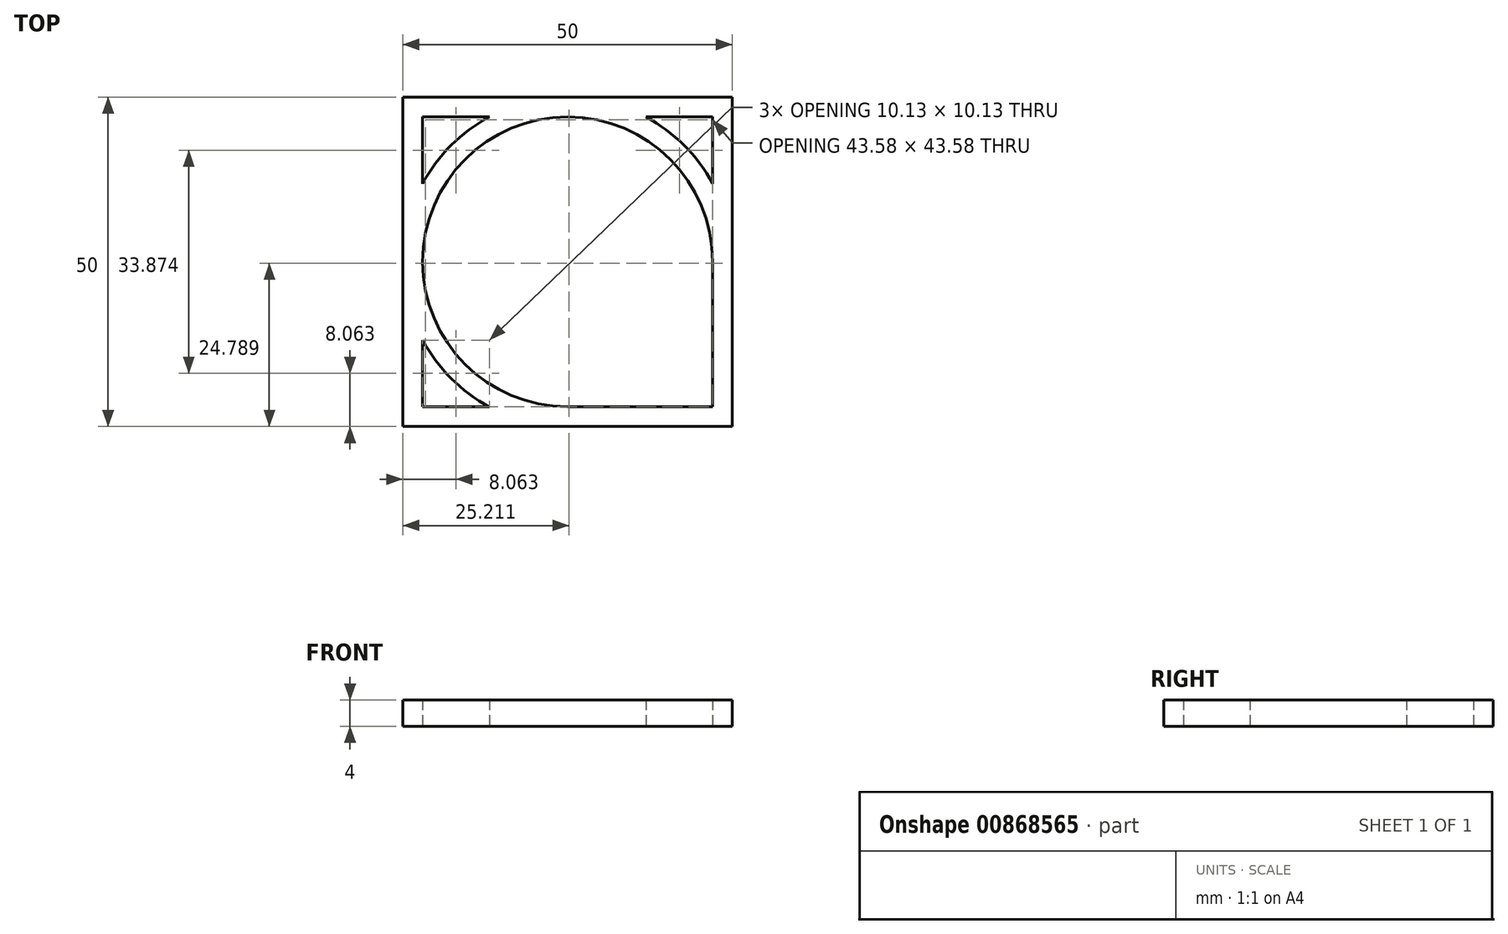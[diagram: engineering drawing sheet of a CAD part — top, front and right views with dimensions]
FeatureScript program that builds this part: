
annotation { "Feature Type Name" : "Feature", "Feature Type Description" : "" }
export const myFeature = defineFeature(function(context is Context, id is Id, definition is map)
    precondition{}
    {
        {
            var Q0;
            Q0=qCreatedBy(makeId("Top.planeOp"),FACE);
            var sketch = newSketch(context, id + "F0", { "sketchPlane" : qUnion([Q0])});
            skLineSegment(sketch, "E0.bottom", {"start": v(0, 0) * mm, "end": v(-50, 0) * mm});
            skLineSegment(sketch, "E0.top", {"start": v(0, 50) * mm, "end": v(-50, 50) * mm});
            skLineSegment(sketch, "E0.left", {"start": v(0, 0) * mm, "end": v(0, 50) * mm});
            skLineSegment(sketch, "E0.right", {"start": v(-50, 0) * mm, "end": v(-50, 50) * mm});
            skLineSegment(sketch, "E1", {"start": v(-25, 61.82) * mm, "end": v(-25, -11.65) * mm, "construction": true});
            skPoint(sketch, "E1.startSnap0", {"position": v(-25, 50) * mm});
            skLineSegment(sketch, "E2", {"start": v(-54.83, 25) * mm, "end": v(11.47, 25) * mm, "construction": true});
            skPoint(sketch, "E2.startSnap0", {"position": v(-50, 25) * mm});
            skCircle(sketch, "E3", {"center": v(-25, 25) * mm, "radius": 25 * mm});
            skCircle(sketch, "E4.0", {"center": v(-25, 25) * mm, "radius": 22 * mm});
            skLineSegment(sketch, "E5.0", {"start": v(-47, 3) * mm, "end": v(-47, 47) * mm});
            skLineSegment(sketch, "E5.1", {"start": v(-3, 3) * mm, "end": v(-47, 3) * mm});
            skLineSegment(sketch, "E5.2", {"start": v(-3, 3) * mm, "end": v(-3, 47) * mm});
            skLineSegment(sketch, "E5.3", {"start": v(-3, 47) * mm, "end": v(-47, 47) * mm});
            skSolve(sketch);
        }
        {
            var Q0;
            {var subQ1=sQuery(id+"F0.wireOp",EDGE,"E0.top");var subQ5=sQuery(id+"F0.wireOp",EDGE,"E0.right");var subQ6=makeQuery(id+"F0.imprint","INTERSECT",VERTEX,{"derivedFrom":[subQ1,subQ5]});Q0=makeQuery(id+"F0.imprint","IMPRINT",FACE,{"disambiguationData":[TD([[makeQuery(id+"F0.imprint","IMPRINT",EDGE,{"disambiguationData":[TD([[subQ6,1.0]])],"derivedFrom":subQ1}),1.0]])]});}
            var Q1;
            {var subQ0=sQuery(id+"F0.wireOp",EDGE,"E3");var subQ1=makeQuery(id+"F0.imprint","INTERSECT",VERTEX,{"derivedFrom":[sQuery(id+"F0.wireOp",EDGE,"E0.right"),subQ0]});Q1=makeQuery(id+"F0.imprint","IMPRINT",FACE,{"disambiguationData":[TD([[makeQuery(id+"F0.imprint","IMPRINT",EDGE,{"disambiguationData":[TD([[subQ1,1.0]])],"derivedFrom":subQ0}),1.0]])]});}
            var Q2;
            {var subQ1=sQuery(id+"F0.wireOp",EDGE,"E0.right");var subQ5=sQuery(id+"F0.wireOp",EDGE,"E0.bottom");var subQ9=makeQuery(id+"F0.imprint","INTERSECT",VERTEX,{"derivedFrom":[subQ5,subQ1]});Q2=makeQuery(id+"F0.imprint","IMPRINT",FACE,{"disambiguationData":[TD([[makeQuery(id+"F0.imprint","IMPRINT",EDGE,{"disambiguationData":[TD([[subQ9,1.0]])],"derivedFrom":subQ5}),-1.0]])]});}
            var Q3;
            {var subQ0=sQuery(id+"F0.wireOp",EDGE,"E3");var subQ1=makeQuery(id+"F0.imprint","INTERSECT",VERTEX,{"derivedFrom":[sQuery(id+"F0.wireOp",EDGE,"E0.bottom"),subQ0]});Q3=makeQuery(id+"F0.imprint","IMPRINT",FACE,{"disambiguationData":[TD([[makeQuery(id+"F0.imprint","IMPRINT",EDGE,{"disambiguationData":[TD([[subQ1,1.0]])],"derivedFrom":subQ0}),1.0]])]});}
            var Q4;
            {var subQ1=sQuery(id+"F0.wireOp",EDGE,"E0.bottom");var subQ7=sQuery(id+"F0.wireOp",EDGE,"E0.left");var subQ10=makeQuery(id+"F0.imprint","INTERSECT",VERTEX,{"derivedFrom":[subQ1,subQ7]});Q4=makeQuery(id+"F0.imprint","IMPRINT",FACE,{"disambiguationData":[TD([[makeQuery(id+"F0.imprint","IMPRINT",EDGE,{"disambiguationData":[TD([[subQ10,-1.0]])],"derivedFrom":subQ1}),-1.0]])]});}
            var Q5;
            {var subQ0=sQuery(id+"F0.wireOp",EDGE,"E3");var subQ1=makeQuery(id+"F0.imprint","INTERSECT",VERTEX,{"derivedFrom":[sQuery(id+"F0.wireOp",EDGE,"E0.left"),subQ0]});Q5=makeQuery(id+"F0.imprint","IMPRINT",FACE,{"disambiguationData":[TD([[makeQuery(id+"F0.imprint","IMPRINT",EDGE,{"disambiguationData":[TD([[subQ1,-1.0]])],"derivedFrom":subQ0}),1.0]])]});}
            var Q6;
            {var subQ1=sQuery(id+"F0.wireOp",EDGE,"E0.left");var subQ5=sQuery(id+"F0.wireOp",EDGE,"E0.top");var subQ9=makeQuery(id+"F0.imprint","INTERSECT",VERTEX,{"derivedFrom":[subQ5,subQ1]});Q6=makeQuery(id+"F0.imprint","IMPRINT",FACE,{"disambiguationData":[TD([[makeQuery(id+"F0.imprint","IMPRINT",EDGE,{"disambiguationData":[TD([[subQ9,-1.0]])],"derivedFrom":subQ5}),1.0]])]});}
            var Q7;
            {var subQ0=sQuery(id+"F0.wireOp",EDGE,"E3");var subQ1=makeQuery(id+"F0.imprint","INTERSECT",VERTEX,{"derivedFrom":[sQuery(id+"F0.wireOp",EDGE,"E0.top"),subQ0]});Q7=makeQuery(id+"F0.imprint","IMPRINT",FACE,{"disambiguationData":[TD([[makeQuery(id+"F0.imprint","IMPRINT",EDGE,{"disambiguationData":[TD([[subQ1,1.0]])],"derivedFrom":subQ0}),1.0]])]});}
            var Q8;
            {var subQ0=sQuery(id+"F0.wireOp",EDGE,"E5.3");var subQ1=sQuery(id+"F0.wireOp",EDGE,"E3");var subQ2=makeQuery(id+"F0.imprint","INTERSECT",VERTEX,{"disambiguationData":[OD(1.0)],"derivedFrom":[subQ1,subQ0]});Q8=makeQuery(id+"F0.imprint","IMPRINT",FACE,{"disambiguationData":[TD([[makeQuery(id+"F0.imprint","IMPRINT",EDGE,{"disambiguationData":[TD([[subQ2,-1.0]])],"derivedFrom":subQ1}),1.0]])]});}
            var Q9;
            {var subQ0=sQuery(id+"F0.wireOp",EDGE,"E5.0");var subQ1=sQuery(id+"F0.wireOp",EDGE,"E3");var subQ2=makeQuery(id+"F0.imprint","INTERSECT",VERTEX,{"disambiguationData":[OD(1.0)],"derivedFrom":[subQ1,subQ0]});Q9=makeQuery(id+"F0.imprint","IMPRINT",FACE,{"disambiguationData":[TD([[makeQuery(id+"F0.imprint","IMPRINT",EDGE,{"disambiguationData":[TD([[subQ2,-1.0]])],"derivedFrom":subQ1}),1.0]])]});}
            var Q10;
            {var subQ0=sQuery(id+"F0.wireOp",EDGE,"E5.1");var subQ1=sQuery(id+"F0.wireOp",EDGE,"E3");var subQ2=makeQuery(id+"F0.imprint","INTERSECT",VERTEX,{"disambiguationData":[OD(1.0)],"derivedFrom":[subQ1,subQ0]});Q10=makeQuery(id+"F0.imprint","IMPRINT",FACE,{"disambiguationData":[TD([[makeQuery(id+"F0.imprint","IMPRINT",EDGE,{"disambiguationData":[TD([[subQ2,-1.0]])],"derivedFrom":subQ1}),1.0]])]});}
            var Q11;
            {var subQ0=sQuery(id+"F0.wireOp",EDGE,"E5.2");var subQ1=sQuery(id+"F0.wireOp",EDGE,"E3");var subQ2=makeQuery(id+"F0.imprint","INTERSECT",VERTEX,{"disambiguationData":[OD(0.0)],"derivedFrom":[subQ1,subQ0]});Q11=makeQuery(id+"F0.imprint","IMPRINT",FACE,{"disambiguationData":[TD([[makeQuery(id+"F0.imprint","IMPRINT",EDGE,{"disambiguationData":[TD([[subQ2,-1.0]])],"derivedFrom":subQ1}),1.0]])]});}
            extrude(context, id + "F1", {"entities" : qUnion([Q0, Q1, Q2, Q3, Q4, Q5, Q6, Q7, Q8, Q9, Q10, Q11]), "depth" : 4 * mm, "offsetDistance" : 25 * mm});
        }
    });
